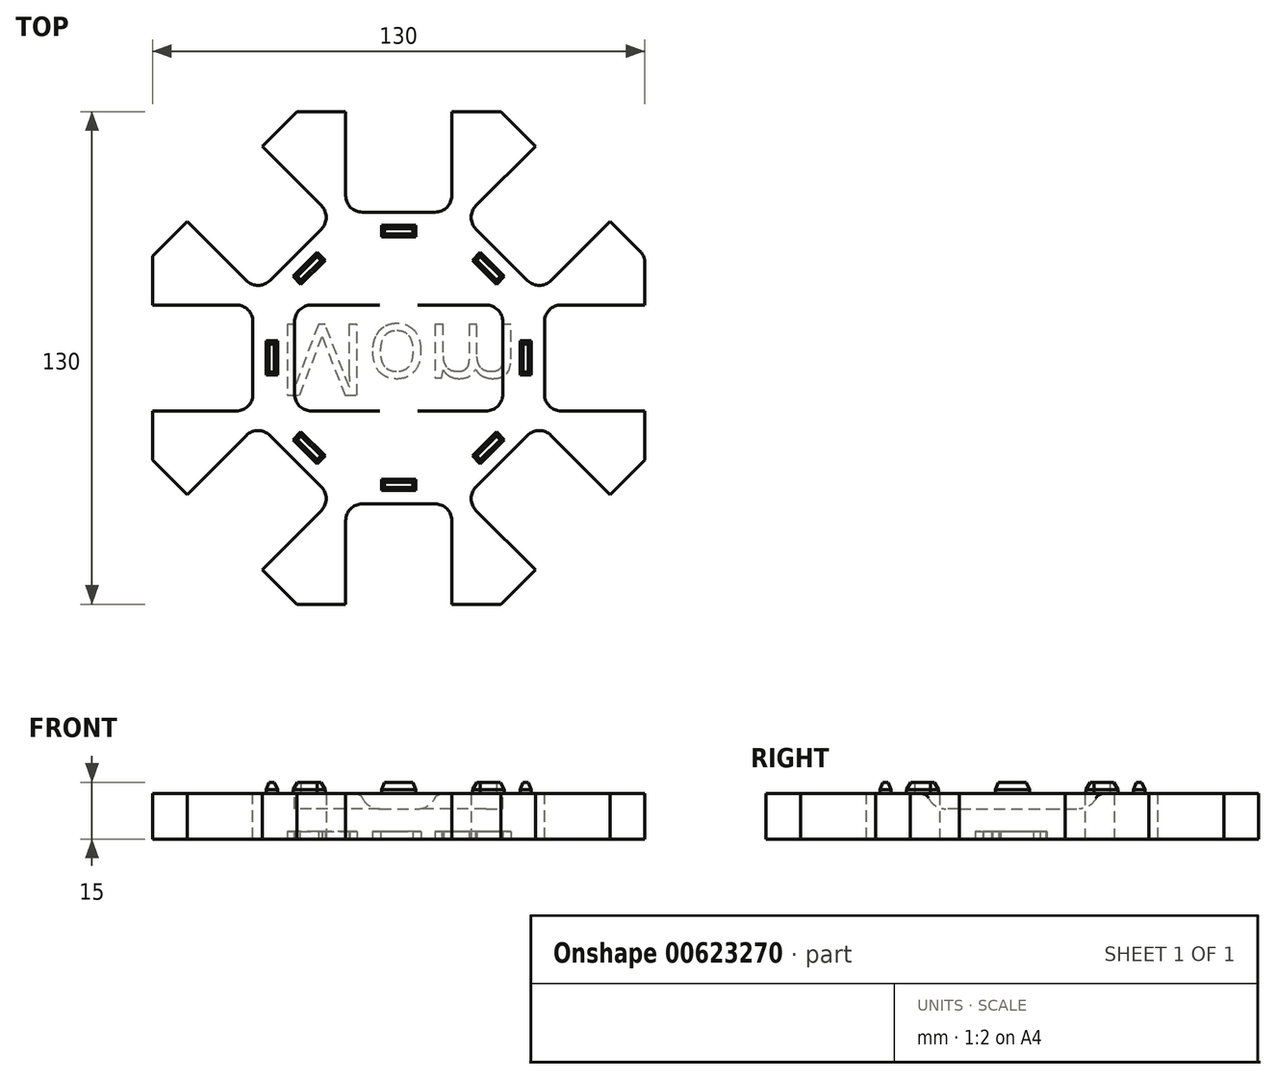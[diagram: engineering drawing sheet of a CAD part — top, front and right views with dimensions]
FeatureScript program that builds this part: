
annotation { "Feature Type Name" : "Feature", "Feature Type Description" : "" }
export const myFeature = defineFeature(function(context is Context, id is Id, definition is map)
    precondition{}
    {
        {
            var Q0;
            Q0=qCreatedBy(makeId("Top.planeOp"),FACE);
            var sketch = newSketch(context, id + "F0", { "sketchPlane" : qUnion([Q0])});
            skCircle(sketch, "E0.cCircle", {"center": v(0, 0) * mm, "radius": 65 * mm, "construction": true});
            skLineSegment(sketch, "E0.0", {"start": v(65, -26.92) * mm, "end": v(26.92, -65) * mm});
            skLineSegment(sketch, "E0.1", {"start": v(26.92, -65) * mm, "end": v(-26.92, -65) * mm});
            skLineSegment(sketch, "E0.2", {"start": v(-26.92, -65) * mm, "end": v(-65, -26.92) * mm});
            skLineSegment(sketch, "E0.3", {"start": v(-65, -26.92) * mm, "end": v(-65, 26.92) * mm});
            skLineSegment(sketch, "E0.4", {"start": v(-65, 26.92) * mm, "end": v(-26.92, 65) * mm});
            skLineSegment(sketch, "E0.5", {"start": v(-26.92, 65) * mm, "end": v(26.92, 65) * mm});
            skLineSegment(sketch, "E0.6", {"start": v(26.92, 65) * mm, "end": v(65, 26.92) * mm});
            skLineSegment(sketch, "E0.7", {"start": v(65, 26.92) * mm, "end": v(65, -26.92) * mm});
            skPoint(sketch, "E0.0.midPoint", {"position": v(45.96, -45.96) * mm});
            skLineSegment(sketch, "E1", {"start": v(0, 65) * mm, "end": v(0, 51.75) * mm, "construction": true});
            skLineSegment(sketch, "E2.bottom", {"start": v(-14, 65) * mm, "end": v(14, 65) * mm});
            skLineSegment(sketch, "E2.top", {"start": v(-14, 38.5) * mm, "end": v(14, 38.5) * mm});
            skLineSegment(sketch, "E2.left", {"start": v(-14, 65) * mm, "end": v(-14, 38.5) * mm});
            skLineSegment(sketch, "E2.right", {"start": v(14, 65) * mm, "end": v(14, 38.5) * mm});
            skPoint(sketch, "E2.middle", {"position": v(0, 51.75) * mm});
            skSolve(sketch);
        }
        {
            var Q0;
            Q0=makeQuery(id+"F0.imprint","IMPRINT",FACE,{"disambiguationData":[TD([[makeQuery(id+"F0.imprint","IMPRINT",EDGE,{"derivedFrom":sQuery(id+"F0.wireOp",EDGE,"E0.0")}),-1.0]])]});
            var Q1;
            Q1=makeQuery(id+"F0.imprint","IMPRINT",FACE,{"disambiguationData":[TD([[makeQuery(id+"F0.imprint","IMPRINT",EDGE,{"derivedFrom":sQuery(id+"F0.wireOp",EDGE,"E2.top")}),1.0]])]});
            extrude(context, id + "F1", {"entities" : qUnion([Q0, Q1]), "depth" : 12 * mm, "offsetDistance" : 25 * mm});
        }
        {
            var Q0;
            Q0=makeQuery(id+"F1.opExtrude","CAP_FACE",FACE,{"disambiguationData":[OSD([sQuery(id+"F0.wireOp",EDGE,"E0.0"),sQuery(id+"F0.wireOp",EDGE,"E0.1"),sQuery(id+"F0.wireOp",EDGE,"E0.2"),sQuery(id+"F0.wireOp",EDGE,"E0.3"),sQuery(id+"F0.wireOp",EDGE,"E0.4"),sQuery(id+"F0.wireOp",EDGE,"E0.5"),sQuery(id+"F0.wireOp",EDGE,"E0.6"),sQuery(id+"F0.wireOp",EDGE,"E0.7"),sQuery(id+"F0.wireOp",EDGE,"E2.bottom")])],"isStart":false});
            var sketch = newSketch(context, id + "F2", { "sketchPlane" : qUnion([Q0])});
            skLineSegment(sketch, "E3", {"start": v(0, 65) * mm, "end": v(0, 51.75) * mm, "construction": true});
            skLineSegment(sketch, "E4.bottom", {"start": v(14, 65) * mm, "end": v(-14, 65) * mm});
            skLineSegment(sketch, "E4.top", {"start": v(14, 38.5) * mm, "end": v(-14, 38.5) * mm});
            skLineSegment(sketch, "E4.left", {"start": v(14, 65) * mm, "end": v(14, 38.5) * mm});
            skLineSegment(sketch, "E4.right", {"start": v(-14, 65) * mm, "end": v(-14, 38.5) * mm});
            skPoint(sketch, "E4.middle", {"position": v(0, 51.75) * mm});
            skLineSegment(sketch, "E5.1.0", {"start": v(-55.86, 36.06) * mm, "end": v(-37.12, 17.32) * mm});
            skLineSegment(sketch, "E5.1.1", {"start": v(-36.06, 55.86) * mm, "end": v(-17.32, 37.12) * mm});
            skLineSegment(sketch, "E5.1.2", {"start": v(-17.32, 37.12) * mm, "end": v(-37.12, 17.32) * mm});
            skLineSegment(sketch, "E5.2.0", {"start": v(-65, -14) * mm, "end": v(-38.5, -14) * mm});
            skLineSegment(sketch, "E5.2.1", {"start": v(-65, 14) * mm, "end": v(-38.5, 14) * mm});
            skLineSegment(sketch, "E5.2.2", {"start": v(-38.5, 14) * mm, "end": v(-38.5, -14) * mm});
            skLineSegment(sketch, "E5.3.0", {"start": v(-36.06, -55.86) * mm, "end": v(-17.32, -37.12) * mm});
            skLineSegment(sketch, "E5.3.1", {"start": v(-55.86, -36.06) * mm, "end": v(-37.12, -17.32) * mm});
            skLineSegment(sketch, "E5.3.2", {"start": v(-37.12, -17.32) * mm, "end": v(-17.32, -37.12) * mm});
            skLineSegment(sketch, "E5.4.0", {"start": v(14, -65) * mm, "end": v(14, -38.5) * mm});
            skLineSegment(sketch, "E5.4.1", {"start": v(-14, -65) * mm, "end": v(-14, -38.5) * mm});
            skLineSegment(sketch, "E5.4.2", {"start": v(-14, -38.5) * mm, "end": v(14, -38.5) * mm});
            skLineSegment(sketch, "E5.5.0", {"start": v(55.86, -36.06) * mm, "end": v(37.12, -17.32) * mm});
            skLineSegment(sketch, "E5.5.1", {"start": v(36.06, -55.86) * mm, "end": v(17.32, -37.12) * mm});
            skLineSegment(sketch, "E5.5.2", {"start": v(17.32, -37.12) * mm, "end": v(37.12, -17.32) * mm});
            skLineSegment(sketch, "E5.6.0", {"start": v(65, 14) * mm, "end": v(38.5, 14) * mm});
            skLineSegment(sketch, "E5.6.1", {"start": v(65, -14) * mm, "end": v(38.5, -14) * mm});
            skLineSegment(sketch, "E5.6.2", {"start": v(38.5, -14) * mm, "end": v(38.5, 14) * mm});
            skLineSegment(sketch, "E5.7.0", {"start": v(36.06, 55.86) * mm, "end": v(17.32, 37.12) * mm});
            skLineSegment(sketch, "E5.7.1", {"start": v(55.86, 36.06) * mm, "end": v(37.12, 17.32) * mm});
            skLineSegment(sketch, "E5.7.2", {"start": v(37.12, 17.32) * mm, "end": v(17.32, 37.12) * mm});
            skPoint(sketch, "E5.center", {"position": v(0, 0) * mm});
            skLineSegment(sketch, "E6.bottom", {"start": v(27.5, -14) * mm, "end": v(-27.5, -14) * mm});
            skLineSegment(sketch, "E6.top", {"start": v(27.5, 14) * mm, "end": v(-27.5, 14) * mm});
            skLineSegment(sketch, "E6.left", {"start": v(27.5, -14) * mm, "end": v(27.5, 14) * mm});
            skLineSegment(sketch, "E6.right", {"start": v(-27.5, -14) * mm, "end": v(-27.5, 14) * mm});
            skLineSegment(sketch, "E7", {"start": v(0, 14) * mm, "end": v(0, -14) * mm});
            skSolve(sketch);
        }
        {
            var Q0;
            Q0=makeQuery(id+"F2.imprint","IMPRINT",FACE,{"disambiguationData":[TD([[makeQuery(id+"F2.imprint","IMPRINT",EDGE,{"derivedFrom":sQuery(id+"F2.wireOp",EDGE,"E4.bottom")}),-1.0]])]});
            var Q1;
            {var subQ0=sQuery(id+"F2.wireOp",EDGE,"E5.1.0");Q1=makeQuery(id+"F2.imprint","IMPRINT",FACE,{"disambiguationData":[TD([[makeQuery(id+"F2.imprint","IMPRINT",EDGE,{"derivedFrom":subQ0}),1.0]])]});}
            var Q2;
            {var subQ0=sQuery(id+"F2.wireOp",EDGE,"E5.2.0");Q2=makeQuery(id+"F2.imprint","IMPRINT",FACE,{"disambiguationData":[TD([[makeQuery(id+"F2.imprint","IMPRINT",EDGE,{"derivedFrom":subQ0}),1.0]])]});}
            var Q3;
            {var subQ0=sQuery(id+"F2.wireOp",EDGE,"E5.7.0");Q3=makeQuery(id+"F2.imprint","IMPRINT",FACE,{"disambiguationData":[TD([[makeQuery(id+"F2.imprint","IMPRINT",EDGE,{"derivedFrom":subQ0}),1.0]])]});}
            var Q4;
            {var subQ0=sQuery(id+"F2.wireOp",EDGE,"E5.6.0");Q4=makeQuery(id+"F2.imprint","IMPRINT",FACE,{"disambiguationData":[TD([[makeQuery(id+"F2.imprint","IMPRINT",EDGE,{"derivedFrom":subQ0}),1.0]])]});}
            var Q5;
            {var subQ0=sQuery(id+"F2.wireOp",EDGE,"E5.5.0");Q5=makeQuery(id+"F2.imprint","IMPRINT",FACE,{"disambiguationData":[TD([[makeQuery(id+"F2.imprint","IMPRINT",EDGE,{"derivedFrom":subQ0}),1.0]])]});}
            var Q6;
            {var subQ0=sQuery(id+"F2.wireOp",EDGE,"E5.4.0");Q6=makeQuery(id+"F2.imprint","IMPRINT",FACE,{"disambiguationData":[TD([[makeQuery(id+"F2.imprint","IMPRINT",EDGE,{"derivedFrom":subQ0}),1.0]])]});}
            var Q7;
            {var subQ0=sQuery(id+"F2.wireOp",EDGE,"E5.3.0");Q7=makeQuery(id+"F2.imprint","IMPRINT",FACE,{"disambiguationData":[TD([[makeQuery(id+"F2.imprint","IMPRINT",EDGE,{"derivedFrom":subQ0}),1.0]])]});}
            extrude(context, id + "F3", {"entities" : qUnion([Q0, Q1, Q2, Q3, Q4, Q5, Q6, Q7]), "operationType" : NewBodyOperationType.REMOVE, "oppositeDirection" : true, "depth" : 25 * mm, "offsetDistance" : 25 * mm});
        }
        {
            var Q0;
            Q0=makeQuery(id+"F3.boolean.opBoolean","COPY",EDGE,{"derivedFrom":makeQuery(id+"F3.opExtrude","SWEPT_EDGE",EDGE,{"disambiguationData":[OSD([sQuery(id+"F2.wireOp",EDGE,"E4.top"),sQuery(id+"F2.wireOp",EDGE,"E4.right")])]})});
            var Q1;
            Q1=makeQuery(id+"F3.boolean.opBoolean","COPY",EDGE,{"derivedFrom":makeQuery(id+"F3.opExtrude","SWEPT_EDGE",EDGE,{"disambiguationData":[OSD([sQuery(id+"F2.wireOp",EDGE,"E5.7.0"),sQuery(id+"F2.wireOp",EDGE,"E5.7.2")])]})});
            var Q2;
            Q2=makeQuery(id+"F3.boolean.opBoolean","COPY",EDGE,{"derivedFrom":makeQuery(id+"F3.opExtrude","SWEPT_EDGE",EDGE,{"disambiguationData":[OSD([sQuery(id+"F2.wireOp",EDGE,"E5.6.0"),sQuery(id+"F2.wireOp",EDGE,"E5.6.2")])]})});
            var Q3;
            Q3=makeQuery(id+"F3.boolean.opBoolean","COPY",EDGE,{"derivedFrom":makeQuery(id+"F3.opExtrude","SWEPT_EDGE",EDGE,{"disambiguationData":[OSD([sQuery(id+"F2.wireOp",EDGE,"E5.5.0"),sQuery(id+"F2.wireOp",EDGE,"E5.5.2")])]})});
            var Q4;
            Q4=makeQuery(id+"F3.boolean.opBoolean","COPY",EDGE,{"derivedFrom":makeQuery(id+"F3.opExtrude","SWEPT_EDGE",EDGE,{"disambiguationData":[OSD([sQuery(id+"F2.wireOp",EDGE,"E5.4.0"),sQuery(id+"F2.wireOp",EDGE,"E5.4.2")])]})});
            var Q5;
            Q5=makeQuery(id+"F3.boolean.opBoolean","COPY",EDGE,{"derivedFrom":makeQuery(id+"F3.opExtrude","SWEPT_EDGE",EDGE,{"disambiguationData":[OSD([sQuery(id+"F2.wireOp",EDGE,"E5.3.0"),sQuery(id+"F2.wireOp",EDGE,"E5.3.2")])]})});
            var Q6;
            Q6=makeQuery(id+"F3.boolean.opBoolean","COPY",EDGE,{"derivedFrom":makeQuery(id+"F3.opExtrude","SWEPT_EDGE",EDGE,{"disambiguationData":[OSD([sQuery(id+"F2.wireOp",EDGE,"E5.2.0"),sQuery(id+"F2.wireOp",EDGE,"E5.2.2")])]})});
            var Q7;
            Q7=makeQuery(id+"F3.boolean.opBoolean","COPY",EDGE,{"derivedFrom":makeQuery(id+"F3.opExtrude","SWEPT_EDGE",EDGE,{"disambiguationData":[OSD([sQuery(id+"F2.wireOp",EDGE,"E5.1.0"),sQuery(id+"F2.wireOp",EDGE,"E5.1.2")])]})});
            var Q8;
            Q8=makeQuery(id+"F3.boolean.opBoolean","COPY",EDGE,{"derivedFrom":makeQuery(id+"F3.opExtrude","SWEPT_EDGE",EDGE,{"disambiguationData":[OSD([sQuery(id+"F2.wireOp",EDGE,"E5.7.1"),sQuery(id+"F2.wireOp",EDGE,"E5.7.2")])]})});
            var Q9;
            Q9=makeQuery(id+"F1.opExtrude","SWEPT_EDGE",EDGE,{"disambiguationData":[OSD([sQuery(id+"F0.wireOp",EDGE,"E0.6"),sQuery(id+"F0.wireOp",EDGE,"E0.7")])]});
            var Q10;
            Q10=makeQuery(id+"F3.boolean.opBoolean","COPY",EDGE,{"derivedFrom":makeQuery(id+"F3.opExtrude","SWEPT_EDGE",EDGE,{"disambiguationData":[OSD([sQuery(id+"F2.wireOp",EDGE,"E5.6.1"),sQuery(id+"F2.wireOp",EDGE,"E5.6.2")])]})});
            var Q11;
            Q11=makeQuery(id+"F3.boolean.opBoolean","COPY",EDGE,{"derivedFrom":makeQuery(id+"F3.opExtrude","SWEPT_EDGE",EDGE,{"disambiguationData":[OSD([sQuery(id+"F2.wireOp",EDGE,"E5.5.1"),sQuery(id+"F2.wireOp",EDGE,"E5.5.2")])]})});
            var Q12;
            Q12=makeQuery(id+"F3.boolean.opBoolean","COPY",EDGE,{"derivedFrom":makeQuery(id+"F3.opExtrude","SWEPT_EDGE",EDGE,{"disambiguationData":[OSD([sQuery(id+"F2.wireOp",EDGE,"E5.4.1"),sQuery(id+"F2.wireOp",EDGE,"E5.4.2")])]})});
            var Q13;
            Q13=makeQuery(id+"F3.boolean.opBoolean","COPY",EDGE,{"derivedFrom":makeQuery(id+"F3.opExtrude","SWEPT_EDGE",EDGE,{"disambiguationData":[OSD([sQuery(id+"F2.wireOp",EDGE,"E5.3.1"),sQuery(id+"F2.wireOp",EDGE,"E5.3.2")])]})});
            var Q14;
            Q14=makeQuery(id+"F3.boolean.opBoolean","COPY",EDGE,{"derivedFrom":makeQuery(id+"F3.opExtrude","SWEPT_EDGE",EDGE,{"disambiguationData":[OSD([sQuery(id+"F2.wireOp",EDGE,"E5.2.1"),sQuery(id+"F2.wireOp",EDGE,"E5.2.2")])]})});
            var Q15;
            Q15=makeQuery(id+"F3.boolean.opBoolean","COPY",EDGE,{"derivedFrom":makeQuery(id+"F3.opExtrude","SWEPT_EDGE",EDGE,{"disambiguationData":[OSD([sQuery(id+"F2.wireOp",EDGE,"E5.1.1"),sQuery(id+"F2.wireOp",EDGE,"E5.1.2")])]})});
            var Q16;
            Q16=makeQuery(id+"F3.boolean.opBoolean","COPY",EDGE,{"derivedFrom":makeQuery(id+"F3.opExtrude","SWEPT_EDGE",EDGE,{"disambiguationData":[OSD([sQuery(id+"F2.wireOp",EDGE,"E4.top"),sQuery(id+"F2.wireOp",EDGE,"E4.left")])]})});
            fillet(context, id + "F4", {"entities" : qUnion([Q0, Q1, Q2, Q3, Q4, Q5, Q6, Q7, Q8, Q9, Q10, Q11, Q12, Q13, Q14, Q15, Q16]), "radius" : 4.4 * mm, "tangentPropagation" : true, "allowEdgeOverflow" : false});
        }
        {
            var Q0;
            Q0=makeQuery(id+"F2.imprint","IMPRINT",FACE,{"disambiguationData":[TD([[makeQuery(id+"F2.imprint","IMPRINT",EDGE,{"derivedFrom":sQuery(id+"F2.wireOp",EDGE,"E6.bottom")}),-1.0]])]});
            extrude(context, id + "F5", {"entities" : qUnion([Q0]), "operationType" : NewBodyOperationType.REMOVE, "oppositeDirection" : true, "depth" : 4 * mm, "offsetDistance" : 25 * mm});
        }
        {
            var Q0;
            Q0=makeQuery(id+"F1.opExtrude","CAP_FACE",FACE,{"disambiguationData":[OSD([sQuery(id+"F0.wireOp",EDGE,"E0.0"),sQuery(id+"F0.wireOp",EDGE,"E0.1"),sQuery(id+"F0.wireOp",EDGE,"E0.2"),sQuery(id+"F0.wireOp",EDGE,"E0.3"),sQuery(id+"F0.wireOp",EDGE,"E0.4"),sQuery(id+"F0.wireOp",EDGE,"E0.5"),sQuery(id+"F0.wireOp",EDGE,"E0.6"),sQuery(id+"F0.wireOp",EDGE,"E0.7")])],"isStart":false});
            var sketch = newSketch(context, id + "F6", { "sketchPlane" : qUnion([Q0])});
            skLineSegment(sketch, "E8", {"start": v(0, 38.5) * mm, "end": v(0, 33.5) * mm, "construction": true});
            skPoint(sketch, "E9.middle", {"position": v(0, 33.5) * mm});
            skLineSegment(sketch, "E10.bottom", {"start": v(4.5, 32) * mm, "end": v(-4.5, 32) * mm});
            skLineSegment(sketch, "E10.top", {"start": v(4.5, 35) * mm, "end": v(-4.5, 35) * mm});
            skLineSegment(sketch, "E10.left", {"start": v(4.5, 32) * mm, "end": v(4.5, 35) * mm});
            skLineSegment(sketch, "E10.right", {"start": v(-4.5, 32) * mm, "end": v(-4.5, 35) * mm});
            skSolve(sketch);
        }
        {
            var Q0;
            {var subQ0=sQuery(id+"F6.wireOp",EDGE,"E9.bottom");Q0=makeQuery(id+"F6.imprint","IMPRINT",FACE,{"disambiguationData":[TD([[makeQuery(id+"F6.imprint","IMPRINT",EDGE,{"derivedFrom":subQ0}),-1.0]])]});}
            var Q1;
            {var subQ5=sQuery(id+"F6.wireOp",EDGE,"E10.left");Q1=makeQuery(id+"F6.imprint","IMPRINT",FACE,{"disambiguationData":[TD([[makeQuery(id+"F6.imprint","IMPRINT",EDGE,{"derivedFrom":subQ5}),1.0]])]});}
            var Q2;
            {var subQ0=sQuery(id+"F6.wireOp",EDGE,"E10.bottom");var subQ1=sQuery(id+"F6.wireOp",EDGE,"E9.left");var subQ2=makeQuery(id+"F6.imprint","INTERSECT",VERTEX,{"derivedFrom":[subQ1,subQ0]});Q2=makeQuery(id+"F6.imprint","IMPRINT",FACE,{"disambiguationData":[TD([[makeQuery(id+"F6.imprint","IMPRINT",EDGE,{"disambiguationData":[TD([[subQ2,-1.0]])],"derivedFrom":subQ1}),1.0]])]});}
            var Q3;
            {var subQ0=sQuery(id+"F6.wireOp",EDGE,"E9.top");Q3=makeQuery(id+"F6.imprint","IMPRINT",FACE,{"disambiguationData":[TD([[makeQuery(id+"F6.imprint","IMPRINT",EDGE,{"derivedFrom":subQ0}),1.0]])]});}
            var Q4;
            {var subQ5=sQuery(id+"F6.wireOp",EDGE,"E10.right");Q4=makeQuery(id+"F6.imprint","IMPRINT",FACE,{"disambiguationData":[TD([[makeQuery(id+"F6.imprint","IMPRINT",EDGE,{"derivedFrom":subQ5}),-1.0]])]});}
            extrude(context, id + "F7", {"entities" : qUnion([Q0, Q1, Q2, Q3, Q4]), "depth" : 3 * mm, "offsetDistance" : 25 * mm});
        }
        {
            var Q0;
            Q0=makeQuery(id+"F1.opExtrude","CAP_FACE",FACE,{"disambiguationData":[OSD([sQuery(id+"F0.wireOp",EDGE,"E0.0"),sQuery(id+"F0.wireOp",EDGE,"E0.1"),sQuery(id+"F0.wireOp",EDGE,"E0.2"),sQuery(id+"F0.wireOp",EDGE,"E0.3"),sQuery(id+"F0.wireOp",EDGE,"E0.4"),sQuery(id+"F0.wireOp",EDGE,"E0.5"),sQuery(id+"F0.wireOp",EDGE,"E0.6"),sQuery(id+"F0.wireOp",EDGE,"E0.7")])],"isStart":false});
            var sketch = newSketch(context, id + "F8", { "sketchPlane" : qUnion([Q0])});
            skPoint(sketch, "E11", {"position": v(0, 0) * mm});
            skCircle(sketch, "E12", {"center": v(0, 0) * mm, "radius": 38.5 * mm, "construction": true});
            skSolve(sketch);
        }
        {
            var Q0;
            Q0=makeQuery(id+"F7.opExtrude","SWEPT_BODY",BODY,{"disambiguationData":[OSD([sQuery(id+"F6.wireOp",EDGE,"E9.bottom"),sQuery(id+"F6.wireOp",EDGE,"E9.top"),sQuery(id+"F6.wireOp",EDGE,"E9.left"),sQuery(id+"F6.wireOp",EDGE,"E9.right"),sQuery(id+"F6.wireOp",EDGE,"E10.bottom"),sQuery(id+"F6.wireOp",EDGE,"E10.top"),sQuery(id+"F6.wireOp",EDGE,"E10.left"),sQuery(id+"F6.wireOp",EDGE,"E10.right")])]});
            var Q1;
            Q1=sQuery(id+"F8.wireOp",EDGE,"E12");
            circularPattern(context, id + "F9", {"entities" : qUnion([Q0]), "axis" : qUnion([Q1]), "angle" : 360 * degree, "instanceCount" : 8, "equalSpace" : true});
        }
        {
            var Q0;
            Q0=makeQuery(id+"F1.opExtrude","CAP_FACE",FACE,{"disambiguationData":[OSD([sQuery(id+"F0.wireOp",EDGE,"E0.0"),sQuery(id+"F0.wireOp",EDGE,"E0.1"),sQuery(id+"F0.wireOp",EDGE,"E0.2"),sQuery(id+"F0.wireOp",EDGE,"E0.3"),sQuery(id+"F0.wireOp",EDGE,"E0.4"),sQuery(id+"F0.wireOp",EDGE,"E0.5"),sQuery(id+"F0.wireOp",EDGE,"E0.6"),sQuery(id+"F0.wireOp",EDGE,"E0.7")])],"isStart":true});
            var sketch = newSketch(context, id + "F10", { "sketchPlane" : qUnion([Q0])});
            skLineSegment(sketch, "E13", {"start": v(0, 0) * mm, "end": v(0, 10) * mm, "construction": true});
            skLineSegment(sketch, "E14", {"start": v(0, 0) * mm, "end": v(-32, 0) * mm, "construction": true});
            skText(sketch, "E15", { "text": "Mom\n", "fontName": "OpenSans-Regular.ttf"});
            const initialGuessF10  = {"E15": [-0.032, -0.00882, 1, 0, 0.01882]};
            skSetInitialGuess(sketch, initialGuessF10);
            skSolve(sketch);
        }
        {
            var Q0;
            Q0=qSketchRegion(id+"F10",true);
            extrude(context, id + "F11", {"entities" : qUnion([Q0]), "operationType" : NewBodyOperationType.REMOVE, "oppositeDirection" : true, "depth" : 2 * mm, "offsetDistance" : 25 * mm});
        }
        {
            var Q0;
            Q0=makeQuery(id+"F5.boolean.opBoolean","COPY",EDGE,{"derivedFrom":makeQuery(id+"F5.opExtrude","SWEPT_EDGE",EDGE,{"disambiguationData":[OSD([sQuery(id+"F2.wireOp",EDGE,"E6.top"),sQuery(id+"F2.wireOp",EDGE,"E6.right")])]})});
            var Q1;
            Q1=makeQuery(id+"F5.boolean.opBoolean","COPY",EDGE,{"derivedFrom":makeQuery(id+"F5.opExtrude","SWEPT_EDGE",EDGE,{"disambiguationData":[OSD([sQuery(id+"F2.wireOp",EDGE,"E6.bottom"),sQuery(id+"F2.wireOp",EDGE,"E6.right")])]})});
            var Q2;
            Q2=makeQuery(id+"F5.boolean.opBoolean","COPY",EDGE,{"derivedFrom":makeQuery(id+"F5.opExtrude","SWEPT_EDGE",EDGE,{"disambiguationData":[OSD([sQuery(id+"F2.wireOp",EDGE,"E6.bottom"),sQuery(id+"F2.wireOp",EDGE,"E6.left")])]})});
            var Q3;
            Q3=makeQuery(id+"F5.boolean.opBoolean","COPY",EDGE,{"derivedFrom":makeQuery(id+"F5.opExtrude","SWEPT_EDGE",EDGE,{"disambiguationData":[OSD([sQuery(id+"F2.wireOp",EDGE,"E6.top"),sQuery(id+"F2.wireOp",EDGE,"E6.left")])]})});
            fillet(context, id + "F12", {"entities" : qUnion([Q0, Q1, Q2, Q3]), "radius" : 4.5 * mm, "tangentPropagation" : true, "allowEdgeOverflow" : false});
        }
        {
            var Q0;
            Q0=makeQuery(id+"F9.opPattern","COPY",EDGE,{"derivedFrom":makeQuery(id+"F7.opExtrude","CAP_EDGE",EDGE,{"disambiguationData":[OSD([sQuery(id+"F6.wireOp",EDGE,"E10.right")])],"isStart":false}),"instanceName":"4"});
            var Q1;
            Q1=makeQuery(id+"F9.opPattern","COPY",EDGE,{"derivedFrom":makeQuery(id+"F7.opExtrude","CAP_EDGE",EDGE,{"disambiguationData":[OSD([sQuery(id+"F6.wireOp",EDGE,"E10.top")])],"isStart":false}),"instanceName":"4"});
            var Q2;
            Q2=makeQuery(id+"F9.opPattern","COPY",EDGE,{"derivedFrom":makeQuery(id+"F7.opExtrude","CAP_EDGE",EDGE,{"disambiguationData":[OSD([sQuery(id+"F6.wireOp",EDGE,"E10.bottom")])],"isStart":false}),"instanceName":"4"});
            var Q3;
            Q3=makeQuery(id+"F9.opPattern","COPY",FACE,{"derivedFrom":makeQuery(id+"F7.opExtrude","CAP_FACE",FACE,{"disambiguationData":[OSD([sQuery(id+"F6.wireOp",EDGE,"E10.bottom"),sQuery(id+"F6.wireOp",EDGE,"E10.top"),sQuery(id+"F6.wireOp",EDGE,"E10.left"),sQuery(id+"F6.wireOp",EDGE,"E10.right")])],"isStart":false}),"instanceName":"4"});
            chamfer(context, id + "F13", {"entities" : qUnion([Q0, Q1, Q2, Q3]), "chamferType" : ChamferType.TWO_OFFSETS, "width1" : 2 * mm, "oppositeDirection" : false, "width2" : .8 * mm, "tangentPropagation" : true});
        }
        {
            var Q0;
            Q0=makeQuery(id+"F9.opPattern","COPY",FACE,{"derivedFrom":makeQuery(id+"F7.opExtrude","CAP_FACE",FACE,{"disambiguationData":[OSD([sQuery(id+"F6.wireOp",EDGE,"E10.bottom"),sQuery(id+"F6.wireOp",EDGE,"E10.top"),sQuery(id+"F6.wireOp",EDGE,"E10.left"),sQuery(id+"F6.wireOp",EDGE,"E10.right")])],"isStart":false}),"instanceName":"5"});
            chamfer(context, id + "F14", {"entities" : qUnion([Q0]), "chamferType" : ChamferType.TWO_OFFSETS, "width1" : 2 * mm, "oppositeDirection" : false, "width2" : .8 * mm, "tangentPropagation" : true});
        }
        {
            var Q0;
            Q0=makeQuery(id+"F9.opPattern","COPY",FACE,{"derivedFrom":makeQuery(id+"F7.opExtrude","CAP_FACE",FACE,{"disambiguationData":[OSD([sQuery(id+"F6.wireOp",EDGE,"E10.bottom"),sQuery(id+"F6.wireOp",EDGE,"E10.top"),sQuery(id+"F6.wireOp",EDGE,"E10.left"),sQuery(id+"F6.wireOp",EDGE,"E10.right")])],"isStart":false}),"instanceName":"6"});
            chamfer(context, id + "F15", {"entities" : qUnion([Q0]), "chamferType" : ChamferType.TWO_OFFSETS, "width1" : 2 * mm, "oppositeDirection" : false, "width2" : .8 * mm, "tangentPropagation" : true});
        }
        {
            var Q0;
            Q0=makeQuery(id+"F9.opPattern","COPY",FACE,{"derivedFrom":makeQuery(id+"F7.opExtrude","CAP_FACE",FACE,{"disambiguationData":[OSD([sQuery(id+"F6.wireOp",EDGE,"E10.bottom"),sQuery(id+"F6.wireOp",EDGE,"E10.top"),sQuery(id+"F6.wireOp",EDGE,"E10.left"),sQuery(id+"F6.wireOp",EDGE,"E10.right")])],"isStart":false}),"instanceName":"7"});
            chamfer(context, id + "F16", {"entities" : qUnion([Q0]), "chamferType" : ChamferType.TWO_OFFSETS, "width1" : 2 * mm, "oppositeDirection" : false, "width2" : .8 * mm, "tangentPropagation" : true});
        }
        {
            var Q0;
            Q0=makeQuery(id+"F7.opExtrude","CAP_FACE",FACE,{"disambiguationData":[OSD([sQuery(id+"F6.wireOp",EDGE,"E10.bottom"),sQuery(id+"F6.wireOp",EDGE,"E10.top"),sQuery(id+"F6.wireOp",EDGE,"E10.left"),sQuery(id+"F6.wireOp",EDGE,"E10.right")])],"isStart":false});
            chamfer(context, id + "F17", {"entities" : qUnion([Q0]), "chamferType" : ChamferType.TWO_OFFSETS, "width1" : 2 * mm, "oppositeDirection" : false, "width2" : .8 * mm, "tangentPropagation" : true});
        }
        {
            var Q0;
            Q0=makeQuery(id+"F9.opPattern","COPY",FACE,{"derivedFrom":makeQuery(id+"F7.opExtrude","CAP_FACE",FACE,{"disambiguationData":[OSD([sQuery(id+"F6.wireOp",EDGE,"E10.bottom"),sQuery(id+"F6.wireOp",EDGE,"E10.top"),sQuery(id+"F6.wireOp",EDGE,"E10.left"),sQuery(id+"F6.wireOp",EDGE,"E10.right")])],"isStart":false}),"instanceName":"1"});
            chamfer(context, id + "F18", {"entities" : qUnion([Q0]), "chamferType" : ChamferType.TWO_OFFSETS, "width1" : 2 * mm, "oppositeDirection" : false, "width2" : .8 * mm, "tangentPropagation" : true});
        }
        {
            var Q0;
            Q0=makeQuery(id+"F9.opPattern","COPY",FACE,{"derivedFrom":makeQuery(id+"F7.opExtrude","CAP_FACE",FACE,{"disambiguationData":[OSD([sQuery(id+"F6.wireOp",EDGE,"E10.bottom"),sQuery(id+"F6.wireOp",EDGE,"E10.top"),sQuery(id+"F6.wireOp",EDGE,"E10.left"),sQuery(id+"F6.wireOp",EDGE,"E10.right")])],"isStart":false}),"instanceName":"2"});
            chamfer(context, id + "F19", {"entities" : qUnion([Q0]), "chamferType" : ChamferType.TWO_OFFSETS, "width1" : 2 * mm, "oppositeDirection" : false, "width2" : .8 * mm, "tangentPropagation" : true});
        }
        {
            var Q0;
            Q0=makeQuery(id+"F9.opPattern","COPY",FACE,{"derivedFrom":makeQuery(id+"F7.opExtrude","CAP_FACE",FACE,{"disambiguationData":[OSD([sQuery(id+"F6.wireOp",EDGE,"E10.bottom"),sQuery(id+"F6.wireOp",EDGE,"E10.top"),sQuery(id+"F6.wireOp",EDGE,"E10.left"),sQuery(id+"F6.wireOp",EDGE,"E10.right")])],"isStart":false}),"instanceName":"3"});
            chamfer(context, id + "F20", {"entities" : qUnion([Q0]), "chamferType" : ChamferType.TWO_OFFSETS, "width1" : 2 * mm, "oppositeDirection" : false, "width2" : .8 * mm, "tangentPropagation" : true});
        }
        {
            var Q0;
            Q0=makeQuery(id+"F1.opExtrude","CAP_FACE",FACE,{"disambiguationData":[OSD([sQuery(id+"F0.wireOp",EDGE,"E0.0"),sQuery(id+"F0.wireOp",EDGE,"E0.1"),sQuery(id+"F0.wireOp",EDGE,"E0.2"),sQuery(id+"F0.wireOp",EDGE,"E0.3"),sQuery(id+"F0.wireOp",EDGE,"E0.4"),sQuery(id+"F0.wireOp",EDGE,"E0.5"),sQuery(id+"F0.wireOp",EDGE,"E0.6"),sQuery(id+"F0.wireOp",EDGE,"E0.7")])],"isStart":false});
            var sketch = newSketch(context, id + "F21", { "sketchPlane" : qUnion([Q0])});
            skLineSegment(sketch, "E16.bottom", {"start": v(10, -22.5) * mm, "end": v(-10, -22.5) * mm});
            skLineSegment(sketch, "E16.top", {"start": v(10, 22.5) * mm, "end": v(-10, 22.5) * mm});
            skLineSegment(sketch, "E16.left", {"start": v(10, -22.5) * mm, "end": v(10, 22.5) * mm});
            skLineSegment(sketch, "E16.right", {"start": v(-10, -22.5) * mm, "end": v(-10, 22.5) * mm});
            skPoint(sketch, "E16.middle", {"position": v(0, 0) * mm});
            skArc(sketch, "E17", {"start": v(10, 14) * mm, "mid": v(0, 22.5) * mm, "end": v(-10, 14) * mm});
            skArc(sketch, "E18", {"start": v(-10, -14) * mm, "mid": v(0, -22.5) * mm, "end": v(10, -14) * mm});
            skSolve(sketch);
        }
        {
            var Q0;
            {var subQ0=sQuery(id+"F21.wireOp",EDGE,"E17");var subQ3=makeQuery(id+"F21.imprint","INTERSECT",VERTEX,{"derivedFrom":[sQuery(id+"F21.wireOp",EDGE,"E16.top"),subQ0]});Q0=makeQuery(id+"F21.imprint","IMPRINT",FACE,{"disambiguationData":[TD([[makeQuery(id+"F21.imprint","IMPRINT",EDGE,{"disambiguationData":[TD([[subQ3,1.0]])],"derivedFrom":subQ0}),1.0]])]});}
            var Q1;
            {var subQ0=sQuery(id+"F21.wireOp",EDGE,"E18");var subQ3=makeQuery(id+"F21.imprint","INTERSECT",VERTEX,{"derivedFrom":[sQuery(id+"F21.wireOp",EDGE,"E16.bottom"),subQ0]});Q1=makeQuery(id+"F21.imprint","IMPRINT",FACE,{"disambiguationData":[TD([[makeQuery(id+"F21.imprint","IMPRINT",EDGE,{"disambiguationData":[TD([[subQ3,1.0]])],"derivedFrom":subQ0}),1.0]])]});}
            extrude(context, id + "F22", {"entities" : qUnion([Q0, Q1]), "operationType" : NewBodyOperationType.REMOVE, "oppositeDirection" : true, "depth" : 4 * mm, "offsetDistance" : 25 * mm});
        }
        {
            var Q0;
            Q0=makeQuery(id+"F22.boolean.opBoolean","COPY",EDGE,{"derivedFrom":makeQuery(id+"F22.opExtrude","CAP_EDGE",EDGE,{"disambiguationData":[OSD([sQuery(id+"F21.wireOp",EDGE,"E17")])],"isStart":false})});
            var Q1;
            Q1=makeQuery(id+"F22.boolean.opBoolean","COPY",EDGE,{"derivedFrom":makeQuery(id+"F22.opExtrude","CAP_EDGE",EDGE,{"disambiguationData":[OSD([sQuery(id+"F21.wireOp",EDGE,"E18")])],"isStart":false})});
            fillet(context, id + "F23", {"entities" : qUnion([Q0, Q1]), "radius" : 5 * mm, "tangentPropagation" : true, "allowEdgeOverflow" : false});
        }
        {
            var Q0;
            Q0=makeQuery(id+"F23.opFillet","BLEND_EDGE",EDGE,{"blendedFrom":[makeQuery(id+"F22.boolean.opBoolean","COPY",EDGE,{"derivedFrom":makeQuery(id+"F22.opExtrude","CAP_EDGE",EDGE,{"disambiguationData":[OSD([sQuery(id+"F21.wireOp",EDGE,"E18")])],"isStart":false})}),makeQuery(id+"F1.opExtrude","CAP_FACE",FACE,{"disambiguationData":[OSD([sQuery(id+"F0.wireOp",EDGE,"E0.0"),sQuery(id+"F0.wireOp",EDGE,"E0.1"),sQuery(id+"F0.wireOp",EDGE,"E0.2"),sQuery(id+"F0.wireOp",EDGE,"E0.3"),sQuery(id+"F0.wireOp",EDGE,"E0.4"),sQuery(id+"F0.wireOp",EDGE,"E0.5"),sQuery(id+"F0.wireOp",EDGE,"E0.6"),sQuery(id+"F0.wireOp",EDGE,"E0.7")])],"isStart":false})],"blendedInto":[makeQuery(id+"F1.opExtrude","CAP_FACE",FACE,{"disambiguationData":[OSD([sQuery(id+"F0.wireOp",EDGE,"E0.0"),sQuery(id+"F0.wireOp",EDGE,"E0.1"),sQuery(id+"F0.wireOp",EDGE,"E0.2"),sQuery(id+"F0.wireOp",EDGE,"E0.3"),sQuery(id+"F0.wireOp",EDGE,"E0.4"),sQuery(id+"F0.wireOp",EDGE,"E0.5"),sQuery(id+"F0.wireOp",EDGE,"E0.6"),sQuery(id+"F0.wireOp",EDGE,"E0.7")])],"isStart":false})]});
            var Q1;
            Q1=makeQuery(id+"F23.opFillet","BLEND_EDGE",EDGE,{"blendedFrom":[makeQuery(id+"F22.boolean.opBoolean","COPY",EDGE,{"derivedFrom":makeQuery(id+"F22.opExtrude","CAP_EDGE",EDGE,{"disambiguationData":[OSD([sQuery(id+"F21.wireOp",EDGE,"E17")])],"isStart":false})}),makeQuery(id+"F1.opExtrude","CAP_FACE",FACE,{"disambiguationData":[OSD([sQuery(id+"F0.wireOp",EDGE,"E0.0"),sQuery(id+"F0.wireOp",EDGE,"E0.1"),sQuery(id+"F0.wireOp",EDGE,"E0.2"),sQuery(id+"F0.wireOp",EDGE,"E0.3"),sQuery(id+"F0.wireOp",EDGE,"E0.4"),sQuery(id+"F0.wireOp",EDGE,"E0.5"),sQuery(id+"F0.wireOp",EDGE,"E0.6"),sQuery(id+"F0.wireOp",EDGE,"E0.7")])],"isStart":false})],"blendedInto":[makeQuery(id+"F1.opExtrude","CAP_FACE",FACE,{"disambiguationData":[OSD([sQuery(id+"F0.wireOp",EDGE,"E0.0"),sQuery(id+"F0.wireOp",EDGE,"E0.1"),sQuery(id+"F0.wireOp",EDGE,"E0.2"),sQuery(id+"F0.wireOp",EDGE,"E0.3"),sQuery(id+"F0.wireOp",EDGE,"E0.4"),sQuery(id+"F0.wireOp",EDGE,"E0.5"),sQuery(id+"F0.wireOp",EDGE,"E0.6"),sQuery(id+"F0.wireOp",EDGE,"E0.7")])],"isStart":false})]});
            fillet(context, id + "F24", {"entities" : qUnion([Q0, Q1]), "radius" : 2 * mm, "tangentPropagation" : true, "allowEdgeOverflow" : false});
        }
    });
